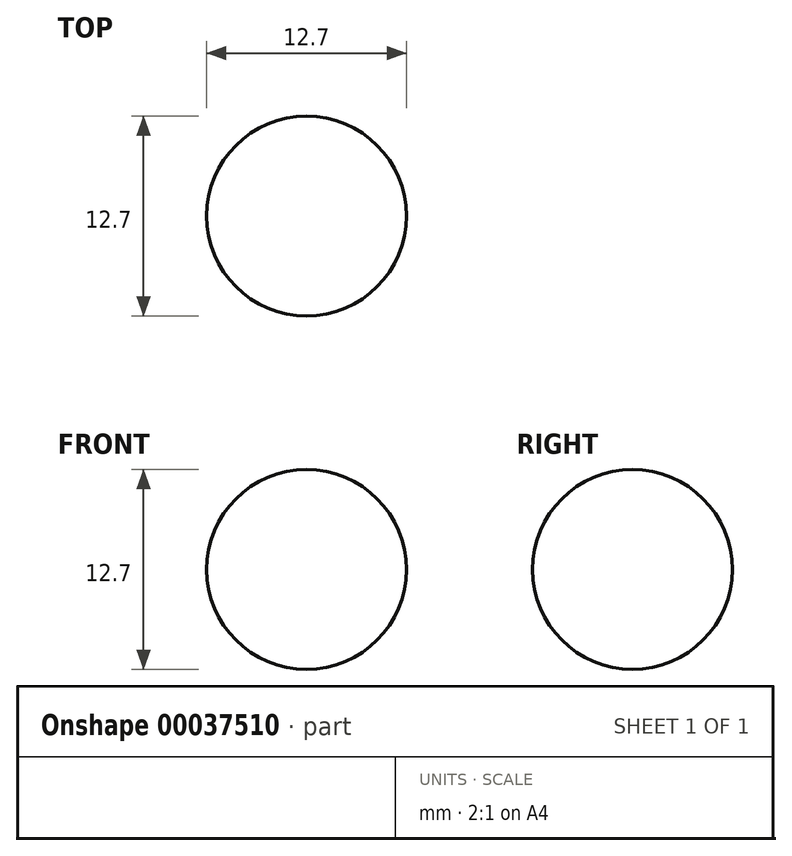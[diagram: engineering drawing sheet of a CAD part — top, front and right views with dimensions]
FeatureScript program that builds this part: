
annotation { "Feature Type Name" : "Feature", "Feature Type Description" : "" }
export const myFeature = defineFeature(function(context is Context, id is Id, definition is map)
    precondition{}
    {
        {
            var Q0;
            Q0=qCreatedBy(makeId("Front.planeOp"),FACE);
            var sketch = newSketch(context, id + "F0", { "sketchPlane" : qUnion([Q0])});
            skPoint(sketch, "E0", {"position": v(0, 12.7) * mm});
            skLineSegment(sketch, "E1", {"start": v(0, 12.7) * mm, "end": v(0, 0) * mm});
            skCircle(sketch, "E2", {"center": v(0, 6.35) * mm, "radius": 6.35 * mm});
            skSolve(sketch);
        }
        {
            var Q0;
            {var subQ1=sQuery(id+"F0.wireOp",EDGE,"E1");Q0=makeQuery(id+"F0.imprint","IMPRINT",FACE,{"disambiguationData":[TD([[makeQuery(id+"F0.imprint","IMPRINT",EDGE,{"derivedFrom":subQ1}),1.0]])]});}
            var Q1;
            Q1=sQuery(id+"F0.wireOp",EDGE,"E1");
            revolve(context, id + "F1", {"entities" : qUnion([Q0]), "axis" : qUnion([Q1]), "revolveType" : RevolveType.FULL});
        }
    });
